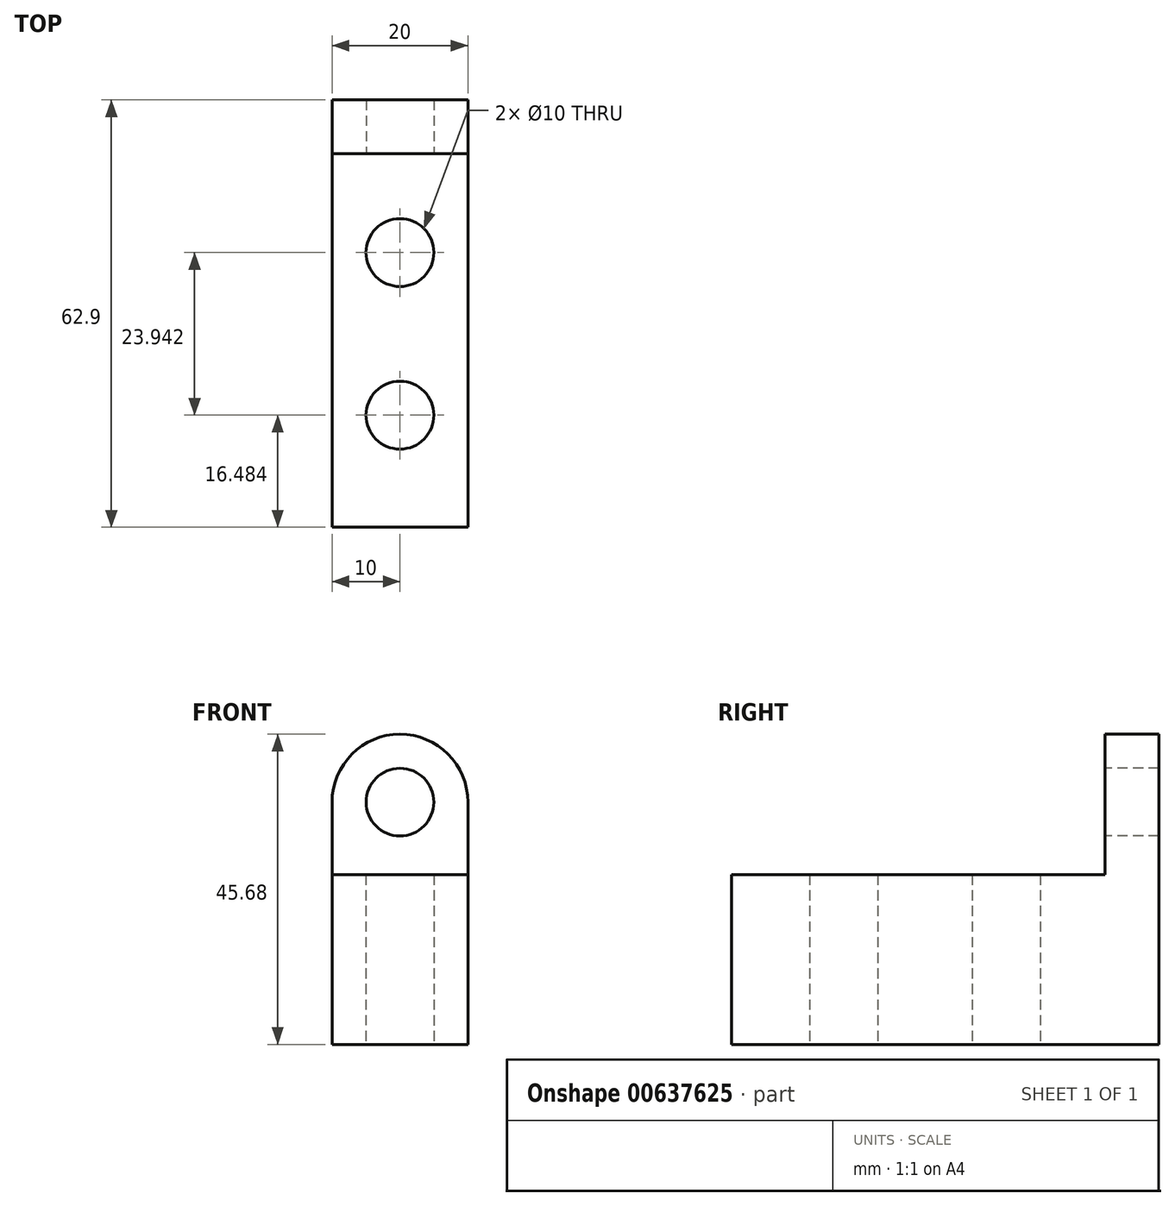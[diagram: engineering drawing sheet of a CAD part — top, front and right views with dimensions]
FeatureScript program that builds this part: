
annotation { "Feature Type Name" : "Feature", "Feature Type Description" : "" }
export const myFeature = defineFeature(function(context is Context, id is Id, definition is map)
    precondition{}
    {
        {
            var Q0;
            Q0=qCreatedBy(makeId("Top.planeOp"),FACE);
            var sketch = newSketch(context, id + "F0", { "sketchPlane" : qUnion([Q0])});
            skLineSegment(sketch, "E0", {"start": v(10, 0) * mm, "end": v(-10, 0) * mm});
            skLineSegment(sketch, "E1", {"start": v(-10, -55) * mm, "end": v(10, -55) * mm});
            skLineSegment(sketch, "E2", {"start": v(10, -55) * mm, "end": v(10, 0) * mm});
            skLineSegment(sketch, "E3", {"start": v(-10, 0) * mm, "end": v(-10, -55) * mm});
            skPoint(sketch, "E4", {"position": v(0, 0) * mm});
            skCircle(sketch, "E5", {"center": v(0, -14.57) * mm, "radius": 5 * mm});
            skCircle(sketch, "E6", {"center": v(0, -38.52) * mm, "radius": 5 * mm});
            skSolve(sketch);
        }
        {
            var Q0;
            Q0 = qSketchRegion(id + "F0", true);
            extrude(context, id + "F1", {"entities" : qUnion([Q0]), "depth" : 25 * mm, "offsetDistance" : 25 * mm});
        }
        {
            var Q0;
            Q0=qCreatedBy(makeId("Front.planeOp"),FACE);
            var sketch = newSketch(context, id + "F2", { "sketchPlane" : qUnion([Q0])});
            skLineSegment(sketch, "E7", {"start": v(-10, 0) * mm, "end": v(-10, 25) * mm});
            skLineSegment(sketch, "E8", {"start": v(-10, 25) * mm, "end": v(10, 25) * mm});
            skLineSegment(sketch, "E9", {"start": v(10, 25) * mm, "end": v(10, 0) * mm});
            skLineSegment(sketch, "E10", {"start": v(10, 0) * mm, "end": v(-10, 0) * mm});
            skLineSegment(sketch, "E11", {"start": v(-10, 25) * mm, "end": v(-10, 35.68) * mm});
            skArc(sketch, "E12", {"start": v(10, 35.68) * mm, "mid": v(0, 45.68) * mm, "end": v(-10, 35.68) * mm});
            skCircle(sketch, "E13", {"center": v(0, 35.68) * mm, "radius": 4.98 * mm});
            skLineSegment(sketch, "E14", {"start": v(10, 25) * mm, "end": v(10, 35.68) * mm});
            skSolve(sketch);
        }
        {
            var Q0;
            Q0 = qSketchRegion(id + "F2", true);
            extrude(context, id + "F3", {"entities" : qUnion([Q0]), "operationType" : NewBodyOperationType.ADD, "oppositeDirection" : true, "depth" : 7.9 * mm, "offsetDistance" : 25 * mm});
        }
    });
